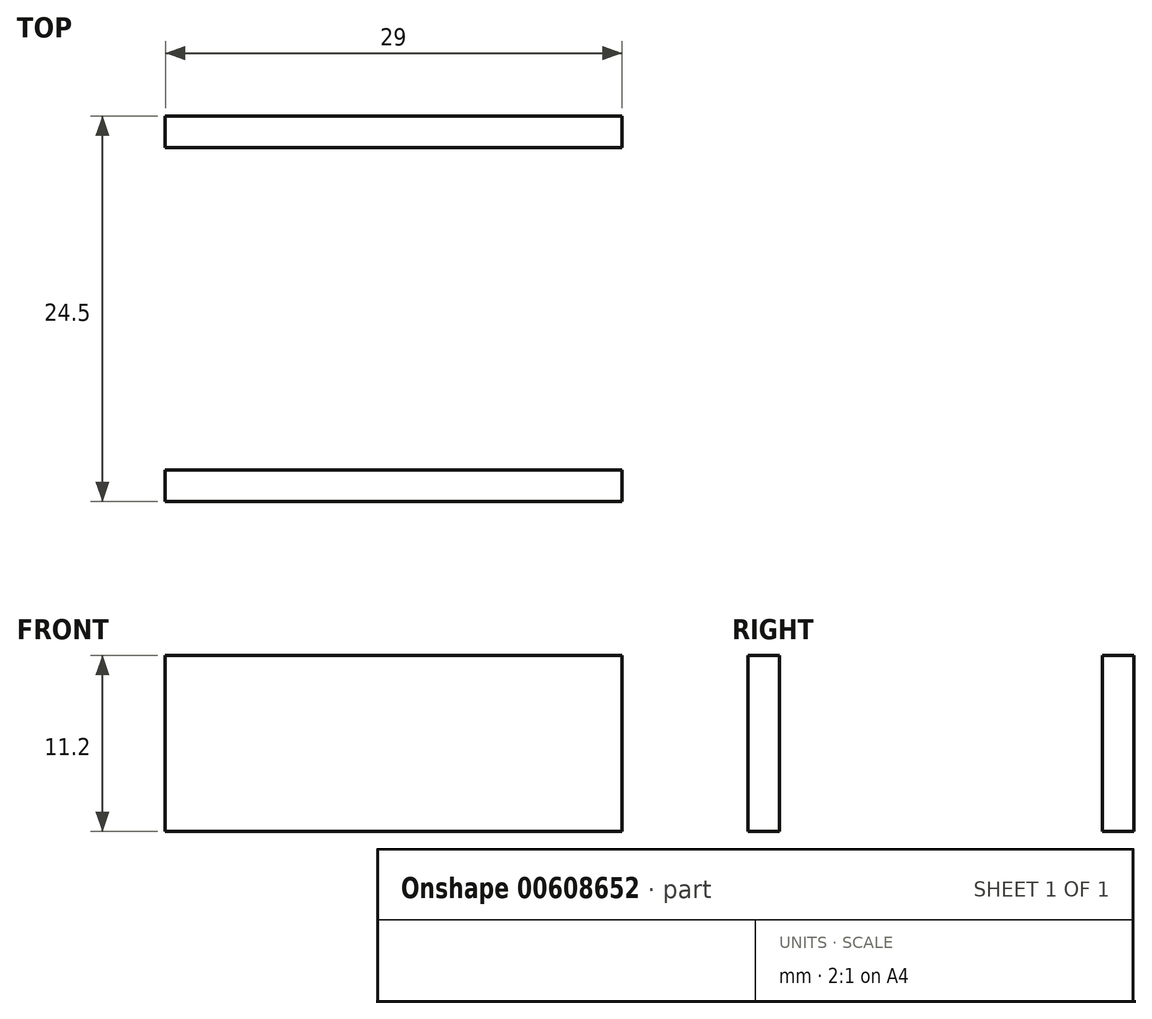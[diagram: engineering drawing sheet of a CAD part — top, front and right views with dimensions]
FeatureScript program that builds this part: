
annotation { "Feature Type Name" : "Feature", "Feature Type Description" : "" }
export const myFeature = defineFeature(function(context is Context, id is Id, definition is map)
    precondition{}
    {
        {
            var Q0;
            Q0=qCreatedBy(makeId("Top.planeOp"),FACE);
            var sketch = newSketch(context, id + "F0", { "sketchPlane" : qUnion([Q0])});
            skLineSegment(sketch, "E0.bottom", {"start": v(-14.76, 15.5) * mm, "end": v(14.24, 15.5) * mm});
            skLineSegment(sketch, "E0.top", {"start": v(-14.76, 13.5) * mm, "end": v(14.24, 13.5) * mm});
            skLineSegment(sketch, "E0.left", {"start": v(-14.76, 15.5) * mm, "end": v(-14.76, 13.5) * mm});
            skLineSegment(sketch, "E0.right", {"start": v(14.24, 15.5) * mm, "end": v(14.24, 13.5) * mm});
            skLineSegment(sketch, "E1.bottom", {"start": v(-14.76, -7) * mm, "end": v(14.24, -7) * mm});
            skLineSegment(sketch, "E1.top", {"start": v(-14.76, -9) * mm, "end": v(14.24, -9) * mm});
            skLineSegment(sketch, "E1.left", {"start": v(-14.76, -7) * mm, "end": v(-14.76, -9) * mm});
            skLineSegment(sketch, "E1.right", {"start": v(14.24, -7) * mm, "end": v(14.24, -9) * mm});
            skSolve(sketch);
        }
        {
            var Q0;
            Q0 = qSketchRegion(id + "F0", true);
            extrude(context, id + "F1", {"entities" : qUnion([Q0]), "depth" : 11.2 * mm, "offsetDistance" : 25 * mm});
        }
    });
